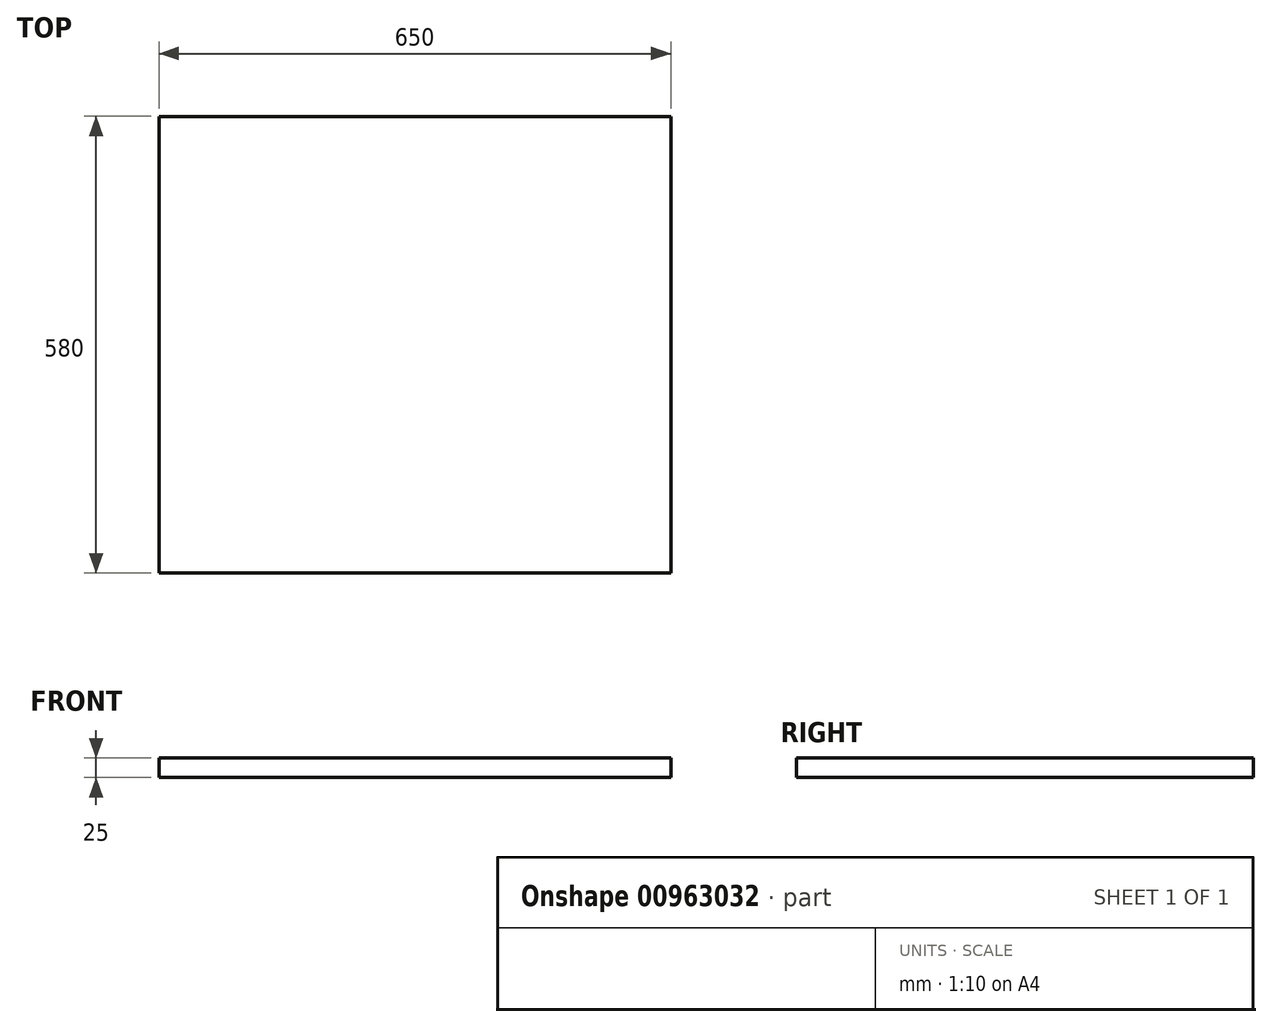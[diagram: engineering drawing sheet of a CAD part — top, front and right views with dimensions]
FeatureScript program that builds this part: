
annotation { "Feature Type Name" : "Feature", "Feature Type Description" : "" }
export const myFeature = defineFeature(function(context is Context, id is Id, definition is map)
    precondition{}
    {
        {
            var Q0;
            Q0=qCreatedBy(makeId("Top.planeOp"),FACE);
            var sketch = newSketch(context, id + "F0", { "sketchPlane" : qUnion([Q0])});
            skLineSegment(sketch, "E0.bottom", {"start": v(-387.06, 218.03) * mm, "end": v(262.94, 218.03) * mm});
            skLineSegment(sketch, "E0.top", {"start": v(-387.06, -361.97) * mm, "end": v(262.94, -361.97) * mm});
            skLineSegment(sketch, "E0.left", {"start": v(-387.06, 218.03) * mm, "end": v(-387.06, -361.97) * mm});
            skLineSegment(sketch, "E0.right", {"start": v(262.94, 218.03) * mm, "end": v(262.94, -361.97) * mm});
            skSolve(sketch);
        }
        {
            var Q0;
            Q0 = qSketchRegion(id + "F0", true);
            extrude(context, id + "F1", {"entities" : qUnion([Q0]), "depth" : 25 * mm, "offsetDistance" : 25 * mm});
        }
        {
            var Q0;
            Q0=makeQuery(id+"F0.imprint","IMPRINT",FACE,{"disambiguationData":[TD([[makeQuery(id+"F0.imprint","IMPRINT",EDGE,{"derivedFrom":sQuery(id+"F0.wireOp",EDGE,"E0.bottom")}),-1.0]])]});
            extrude(context, id + "F2", {"entities" : qUnion([Q0]), "operationType" : NewBodyOperationType.ADD, "depth" : 25 * mm, "offsetDistance" : 25 * mm});
        }
    });
